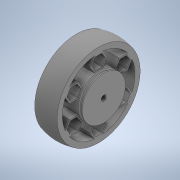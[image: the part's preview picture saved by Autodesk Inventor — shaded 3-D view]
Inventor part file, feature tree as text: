
AUTODESK INVENTOR PART (.ipt)
format: ipt  version: 2020 (Build 240168000, 168)  size: 312,320 bytes
history: native  units: in
note: dims shown in document units (in); Inventor stores cm internally (conversion verified against a paired STEP export)
features: sketch x4, extrude x2, revolve x2, projected_geometry x1
ambient origin geometry x8: Origin, YZ Plane, XZ Plane, XY Plane, X Axis, Y Axis, Z Axis, Center Point
bodies: Solid1 (feature_tree)
feature tree (9):
  extrude  "Extrusion1"  Depth=0.1181in
  sketch  "Sketch3"  dims[d6=0.9843in d7=0.1181in]
  revolve  "Revolution1"  [1 undecoded]
  extrude  "Extrusion2"  Depth=0.1181in
  revolve  "Revolution2"  [1 undecoded]
  sketch  "Sketch1"  dims[d0=0.1181in d1=0.0394in]
  sketch  "Sketch2"  dims[d3=1.8898in d4=0.1181in]
  projected_geometry  "Projected Loop1"
  sketch  "Sketch4"  dims[d8=0.0in d9=1.8898in d10=0.1181in d11=0.0315in d12=2.3622in d14=360.0deg d16=0.5118in d17=0.0in d19=90.0deg d20=0.0394in d22=60.0deg d24=0.0394in d25=90.0deg d26=60.0deg]
note: 2 required parameter values undecoded (feature->parameter linkage not recoverable at this tier; creation-order binding heuristic only, values carry confidence <= 0.55)
